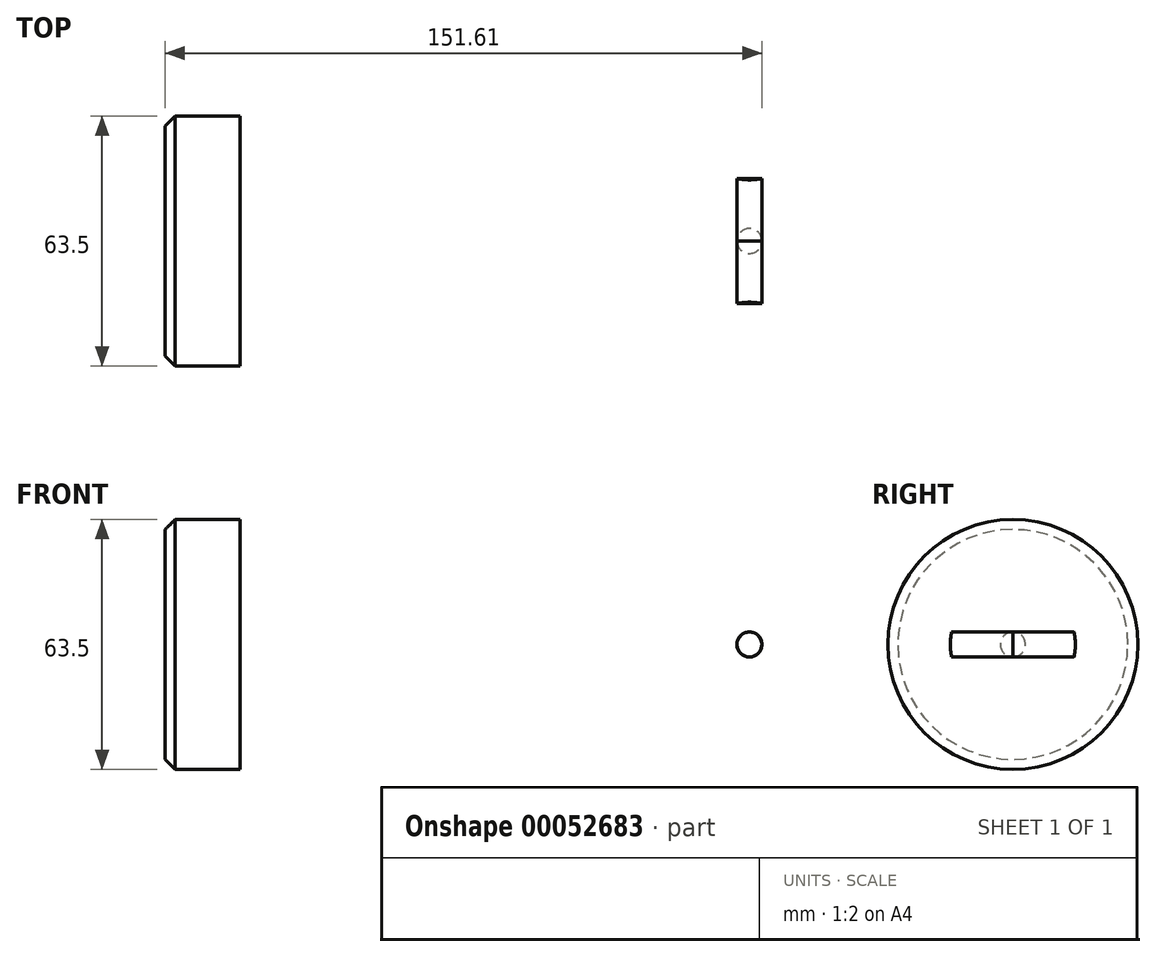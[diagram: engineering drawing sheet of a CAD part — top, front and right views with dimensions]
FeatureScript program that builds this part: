
annotation { "Feature Type Name" : "Feature", "Feature Type Description" : "" }
export const myFeature = defineFeature(function(context is Context, id is Id, definition is map)
    precondition{}
    {
        {
            var Q0;
            Q0=qCreatedBy(makeId("Front.planeOp"),FACE);
            var sketch = newSketch(context, id + "F0", { "sketchPlane" : qUnion([Q0])});
            skLineSegment(sketch, "E0.bottom", {"start": v(-76.2, -15.88) * mm, "end": v(76.2, -15.88) * mm});
            skLineSegment(sketch, "E0.top", {"start": v(-76.2, 15.88) * mm, "end": v(76.2, 15.88) * mm});
            skLineSegment(sketch, "E0.left", {"start": v(-76.2, -15.88) * mm, "end": v(-76.2, 15.88) * mm});
            skLineSegment(sketch, "E0.right", {"start": v(76.2, -15.88) * mm, "end": v(76.2, 15.88) * mm});
            skPoint(sketch, "E0.middle", {"position": v(0, 0) * mm});
            skLineSegment(sketch, "E1.bottom", {"start": v(-76.2, 31.75) * mm, "end": v(-95.25, 31.75) * mm});
            skLineSegment(sketch, "E1.top", {"start": v(-76.2, -31.75) * mm, "end": v(-95.25, -31.75) * mm});
            skLineSegment(sketch, "E1.left", {"start": v(-76.2, 31.75) * mm, "end": v(-76.2, -31.75) * mm});
            skLineSegment(sketch, "E1.right", {"start": v(-95.25, 31.75) * mm, "end": v(-95.25, -31.75) * mm});
            skPoint(sketch, "E1.middle", {"position": v(-85.73, 0) * mm});
            skPoint(sketch, "E1.middle.positionSnap0", {"position": v(-76.2, 0) * mm});
            skPoint(sketch, "E1.centerSnap0", {"position": v(-76.2, 0) * mm});
            skLineSegment(sketch, "E2", {"start": v(76.2, 0) * mm, "end": v(-95.25, 0) * mm});
            skPoint(sketch, "E3", {"position": v(53.19, 0) * mm});
            skCircle(sketch, "E4", {"center": v(53.19, 0) * mm, "radius": 3.18 * mm});
            skSolve(sketch);
        }
        {
            var Q0;
            {var subQ0=sQuery(id+"F0.wireOp",EDGE,"E0.top");Q0=makeQuery(id+"F0.imprint","IMPRINT",FACE,{"disambiguationData":[TD([[makeQuery(id+"F0.imprint","IMPRINT",EDGE,{"derivedFrom":subQ0}),-1.0]])]});}
            var Q1;
            {var subQ1=sQuery(id+"F0.wireOp",EDGE,"E1.bottom");Q1=makeQuery(id+"F0.imprint","IMPRINT",FACE,{"disambiguationData":[TD([[makeQuery(id+"F0.imprint","IMPRINT",EDGE,{"derivedFrom":subQ1}),1.0]])]});}
            var Q2;
            Q2=sQuery(id+"F0.wireOp",EDGE,"E2");
            revolve(context, id + "F1", {"surfaceOperationType" : NewSurfaceOperationType.NEW, "entities" : qUnion([Q0, Q1]), "axis" : qUnion([Q2]), "revolveType" : RevolveType.FULL});
        }
        {
            var Q0;
            {var subQ0=sQuery(id+"F0.wireOp",EDGE,"E4");var subQ1=sQuery(id+"F0.wireOp",EDGE,"E2");var subQ2=makeQuery(id+"F0.imprint","INTERSECT",VERTEX,{"disambiguationData":[OD(0.0)],"derivedFrom":[subQ1,subQ0]});Q0=makeQuery(id+"F0.imprint","IMPRINT",FACE,{"disambiguationData":[TD([[makeQuery(id+"F0.imprint","IMPRINT",EDGE,{"disambiguationData":[TD([[subQ2,-1.0]])],"derivedFrom":subQ1}),1.0]])]});}
            var Q1;
            {var subQ0=sQuery(id+"F0.wireOp",EDGE,"E4");var subQ1=sQuery(id+"F0.wireOp",EDGE,"E2");var subQ2=makeQuery(id+"F0.imprint","INTERSECT",VERTEX,{"disambiguationData":[OD(0.0)],"derivedFrom":[subQ1,subQ0]});Q1=makeQuery(id+"F0.imprint","IMPRINT",FACE,{"disambiguationData":[TD([[makeQuery(id+"F0.imprint","IMPRINT",EDGE,{"disambiguationData":[TD([[subQ2,-1.0]])],"derivedFrom":subQ1}),-1.0]])]});}
            extrude(context, id + "F2", {"entities" : qUnion([Q0, Q1]), "operationType" : NewBodyOperationType.REMOVE, "oppositeDirection" : true, "depth" : 50.8 * mm, "offsetDistance" : 25.4 * mm, "symmetric" : true});
        }
        {
            var Q0;
            Q0=makeQuery(id+"F1.opRevolve","SWEPT_EDGE",EDGE,{"disambiguationData":[OSD([sQuery(id+"F0.wireOp",EDGE,"E0.top"),sQuery(id+"F0.wireOp",EDGE,"E0.right")])]});
            var Q1;
            Q1=makeQuery(id+"F1.opRevolve","SWEPT_EDGE",EDGE,{"disambiguationData":[OSD([sQuery(id+"F0.wireOp",EDGE,"E1.bottom"),sQuery(id+"F0.wireOp",EDGE,"E1.right")])]});
            chamfer(context, id + "F3", {"entities" : qUnion([Q0, Q1]), "width" : 2.54 * mm, "tangentPropagation" : true});
        }
    });
